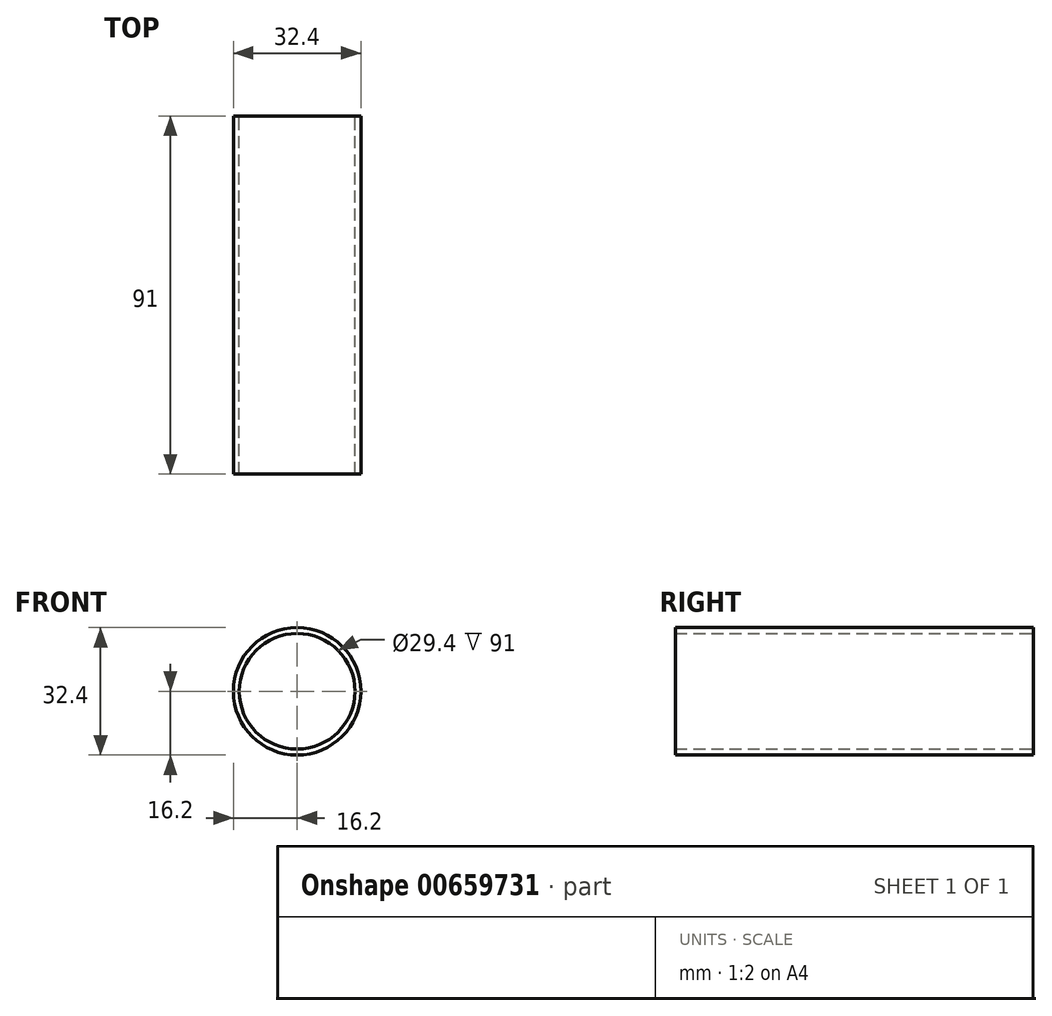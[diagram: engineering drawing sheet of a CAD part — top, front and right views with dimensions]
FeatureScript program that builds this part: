
annotation { "Feature Type Name" : "Feature", "Feature Type Description" : "" }
export const myFeature = defineFeature(function(context is Context, id is Id, definition is map)
    precondition{}
    {
        {
            var Q0;
            Q0=qCreatedBy(makeId("Front.planeOp"),FACE);
            var sketch = newSketch(context, id + "F0", { "sketchPlane" : qUnion([Q0])});
            skCircle(sketch, "E0", {"center": v(0, 0) * mm, "radius": 14.7 * mm});
            skCircle(sketch, "E1", {"center": v(0, 0) * mm, "radius": 16.2 * mm});
            skSolve(sketch);
        }
        {
            var Q0;
            Q0=makeQuery(id+"F0.imprint","IMPRINT",FACE,{"disambiguationData":[TD([[makeQuery(id+"F0.imprint","IMPRINT",EDGE,{"derivedFrom":sQuery(id+"F0.wireOp",EDGE,"E0")}),-1.0]])]});
            extrude(context, id + "F1", {"entities" : qUnion([Q0]), "depth" : 91 * mm, "offsetDistance" : 25 * mm});
        }
    });
